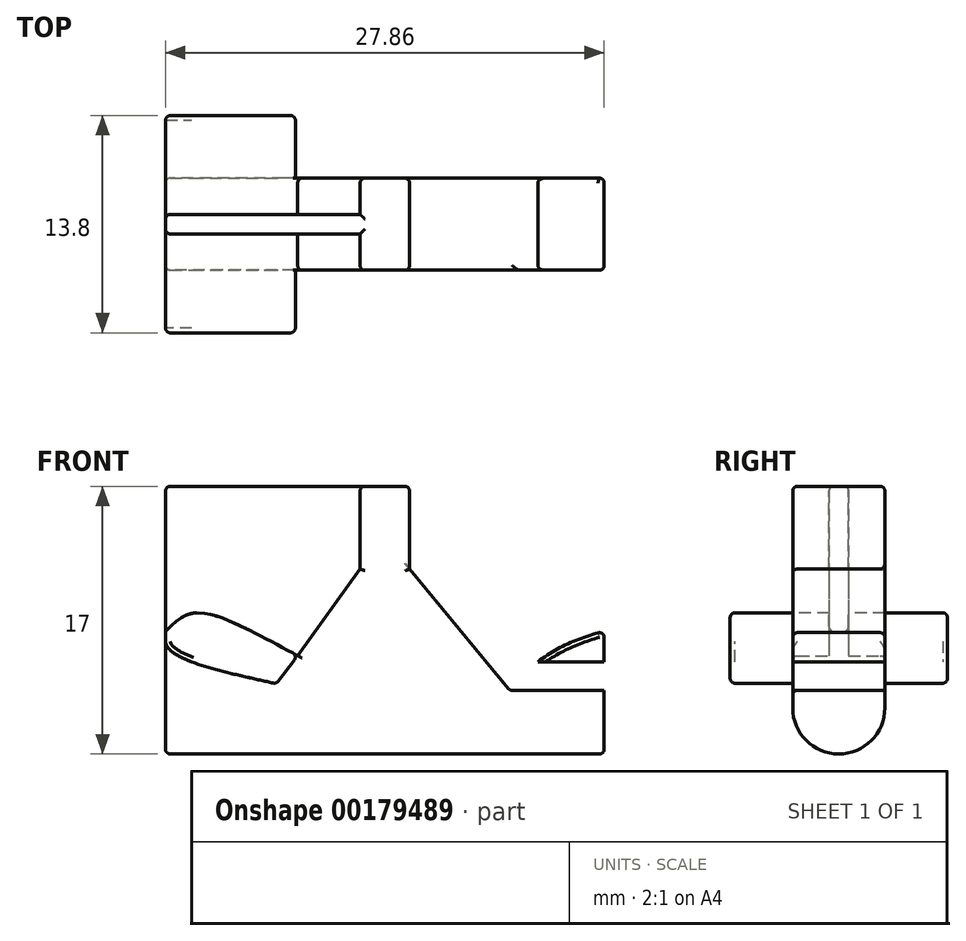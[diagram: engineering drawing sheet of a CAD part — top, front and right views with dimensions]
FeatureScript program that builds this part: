
annotation { "Feature Type Name" : "Feature", "Feature Type Description" : "" }
export const myFeature = defineFeature(function(context is Context, id is Id, definition is map)
    precondition{}
    {
        {
            var Q0;
            Q0=qCreatedBy(makeId("Front.planeOp"),FACE);
            var sketch = newSketch(context, id + "F0", { "sketchPlane" : qUnion([Q0])});
            skLineSegment(sketch, "E0.bottom", {"start": v(1.57, 8.26) * mm, "end": v(-1.57, 8.26) * mm});
            skLineSegment(sketch, "E0.top", {"start": v(1.57, 13.52) * mm, "end": v(-1.57, 13.52) * mm});
            skLineSegment(sketch, "E0.left", {"start": v(1.57, 8.26) * mm, "end": v(1.57, 13.52) * mm});
            skLineSegment(sketch, "E0.right", {"start": v(-1.57, 8.26) * mm, "end": v(-1.57, 13.52) * mm});
            skPoint(sketch, "E0.middle", {"position": v(0, 10.89) * mm});
            skLineSegment(sketch, "E1.bottom", {"start": v(13.93, -0.56) * mm, "end": v(-13.93, -0.56) * mm});
            skLineSegment(sketch, "E1.top", {"start": v(13.93, 0.56) * mm, "end": v(-13.93, 0.56) * mm});
            skLineSegment(sketch, "E1.left", {"start": v(13.93, -0.56) * mm, "end": v(13.93, 0.56) * mm});
            skLineSegment(sketch, "E1.right", {"start": v(-13.93, -0.56) * mm, "end": v(-13.93, 0.56) * mm});
            skPoint(sketch, "E1.middle", {"position": v(0, 0) * mm});
            skLineSegment(sketch, "E2", {"start": v(13.93, 0.56) * mm, "end": v(13.93, 4.32) * mm});
            skLineSegment(sketch, "E3", {"start": v(1.57, 8.26) * mm, "end": v(7.95, 0.56) * mm});
            skLineSegment(sketch, "E4", {"start": v(-1.57, 8.26) * mm, "end": v(-5.54, 2.76) * mm});
            skLineSegment(sketch, "E5", {"start": v(-13.93, 0.56) * mm, "end": v(-13.93, 4.32) * mm});
            skFitSpline(sketch, "E6", {"points": [v(-13.93, 4.32) * mm, v(-5.54, 2.76) * mm], "startDerivative": vector(5.32, 5.39) * mm, "endDerivative": vector(18.06, -9.8) * mm});
            skFitSpline(sketch, "E7", {"points": [v(7.95, 0.56) * mm, v(13.93, 4.32) * mm], "startDerivative": vector(5.08, 6.59) * mm, "endDerivative": vector(7.3, 1.91) * mm});
            skLineSegment(sketch, "E8.bottom", {"start": v(13.93, -3.48) * mm, "end": v(-13.93, -3.48) * mm});
            skLineSegment(sketch, "E8.top", {"start": v(13.93, 2.37) * mm, "end": v(-13.93, 2.37) * mm});
            skLineSegment(sketch, "E8.left", {"start": v(13.93, -3.48) * mm, "end": v(13.93, 2.37) * mm});
            skLineSegment(sketch, "E8.right", {"start": v(-13.93, -3.48) * mm, "end": v(-13.93, 2.37) * mm});
            skPoint(sketch, "E8.middle", {"position": v(0, -0.56) * mm});
            skLineSegment(sketch, "E9", {"start": v(-5.54, 2.76) * mm, "end": v(-6.9, 0.98) * mm});
            skFitSpline(sketch, "E10", {"points": [v(-13.93, 3.67) * mm, v(-6.9, 0.98) * mm], "startDerivative": vector(0, -3.91) * mm, "endDerivative": vector(7.3, -1.73) * mm});
            skLineSegment(sketch, "E11.bottom", {"start": v(-1.57, 13.52) * mm, "end": v(-13.93, 13.52) * mm});
            skLineSegment(sketch, "E11.top", {"start": v(-1.57, 0.56) * mm, "end": v(-13.93, 0.56) * mm});
            skLineSegment(sketch, "E11.left", {"start": v(-1.57, 13.52) * mm, "end": v(-1.57, 0.56) * mm});
            skLineSegment(sketch, "E11.right", {"start": v(-13.93, 13.52) * mm, "end": v(-13.93, 0.56) * mm});
            skSolve(sketch);
        }
        {
            var Q0;
            Q0=makeQuery(id+"F0.imprint","IMPRINT",FACE,{"disambiguationData":[TD([[makeQuery(id+"F0.imprint","IMPRINT",EDGE,{"derivedFrom":sQuery(id+"F0.wireOp",EDGE,"E0.bottom")}),-1.0]])]});
            var Q1;
            {var subQ6=sQuery(id+"F0.wireOp",EDGE,"E0.bottom");Q1=makeQuery(id+"F0.imprint","IMPRINT",FACE,{"disambiguationData":[TD([[makeQuery(id+"F0.imprint","IMPRINT",EDGE,{"derivedFrom":subQ6}),1.0]])]});}
            var Q2;
            {var subQ1=sQuery(id+"F0.wireOp",EDGE,"E8.top");var subQ5=sQuery(id+"F0.wireOp",EDGE,"E3");var subQ6=makeQuery(id+"F0.imprint","INTERSECT",VERTEX,{"derivedFrom":[subQ5,subQ1]});Q2=makeQuery(id+"F0.imprint","IMPRINT",FACE,{"disambiguationData":[TD([[makeQuery(id+"F0.imprint","IMPRINT",EDGE,{"disambiguationData":[TD([[subQ6,-1.0]])],"derivedFrom":subQ1}),1.0]])]});}
            var Q3;
            {var subQ0=sQuery(id+"F0.wireOp",EDGE,"E8.left");var subQ1=sQuery(id+"F0.wireOp",EDGE,"E1.top");var subQ2=makeQuery(id+"F0.imprint","INTERSECT",VERTEX,{"derivedFrom":[subQ1,subQ0]});Q3=makeQuery(id+"F0.imprint","IMPRINT",FACE,{"disambiguationData":[TD([[makeQuery(id+"F0.imprint","IMPRINT",EDGE,{"disambiguationData":[TD([[subQ2,-1.0]])],"derivedFrom":subQ1}),-1.0]])]});}
            var Q4;
            {var subQ1=sQuery(id+"F0.wireOp",EDGE,"E1.bottom");Q4=makeQuery(id+"F0.imprint","IMPRINT",FACE,{"disambiguationData":[TD([[makeQuery(id+"F0.imprint","IMPRINT",EDGE,{"derivedFrom":subQ1}),-1.0]])]});}
            var Q5;
            {var subQ1=sQuery(id+"F0.wireOp",EDGE,"E5");var subQ3=sQuery(id+"F0.wireOp",EDGE,"E10");var subQ4=makeQuery(id+"F0.imprint","INTERSECT",VERTEX,{"derivedFrom":[subQ1,subQ3]});Q5=makeQuery(id+"F0.imprint","IMPRINT",FACE,{"disambiguationData":[TD([[makeQuery(id+"F0.imprint","IMPRINT",EDGE,{"disambiguationData":[TD([[subQ4,-1.0]])],"derivedFrom":subQ3}),-1.0]])]});}
            var Q6;
            {var subQ0=sQuery(id+"F0.wireOp",EDGE,"E2");Q6=makeQuery(id+"F0.imprint","IMPRINT",FACE,{"disambiguationData":[TD([[makeQuery(id+"F0.imprint","IMPRINT",EDGE,{"derivedFrom":subQ0}),1.0]])]});}
            extrude(context, id + "F1", {"entities" : qUnion([Q0, Q1, Q2, Q3, Q4, Q5, Q6]), "endBound" : BoundingType.SYMMETRIC, "depth" : 5.85 * mm});
        }
        {
            var Q0;
            {var subQ5=sQuery(id+"F0.wireOp",EDGE,"E6");Q0=makeQuery(id+"F0.imprint","IMPRINT",FACE,{"disambiguationData":[TD([[makeQuery(id+"F0.imprint","IMPRINT",EDGE,{"derivedFrom":subQ5}),-1.0]])]});}
            var Q1;
            {var subQ0=sQuery(id+"F0.wireOp",EDGE,"E9");var subQ1=sQuery(id+"F0.wireOp",EDGE,"E8.top");var subQ2=makeQuery(id+"F0.imprint","INTERSECT",VERTEX,{"derivedFrom":[subQ1,subQ0]});Q1=makeQuery(id+"F0.imprint","IMPRINT",FACE,{"disambiguationData":[TD([[makeQuery(id+"F0.imprint","IMPRINT",EDGE,{"disambiguationData":[TD([[subQ2,-1.0]])],"derivedFrom":subQ1}),1.0]])]});}
            extrude(context, id + "F2", {"entities" : qUnion([Q0, Q1]), "operationType" : NewBodyOperationType.ADD, "endBound" : BoundingType.SYMMETRIC, "depth" : 13.8 * mm});
        }
        {
            var Q0;
            {var subQ0=sQuery(id+"F0.wireOp",EDGE,"E1.bottom");Q0=makeQuery(id+"F0.imprint","IMPRINT",FACE,{"disambiguationData":[TD([[makeQuery(id+"F0.imprint","IMPRINT",EDGE,{"derivedFrom":subQ0}),1.0]])]});}
            var Q1;
            Q1=sQuery(id+"F0.wireOp",EDGE,"E1.bottom");
            revolve(context, id + "F3", {"operationType" : NewBodyOperationType.ADD, "entities" : qUnion([Q0]), "axis" : qUnion([Q1]), "revolveType" : RevolveType.SYMMETRIC, "angle" : 180 * degree});
        }
        {
            var Q0;
            {var subQ4=sQuery(id+"F0.wireOp",EDGE,"E4");Q0=makeQuery(id+"F0.imprint","IMPRINT",FACE,{"disambiguationData":[TD([[makeQuery(id+"F0.imprint","IMPRINT",EDGE,{"derivedFrom":subQ4}),-1.0]])]});}
            extrude(context, id + "F4", {"entities" : qUnion([Q0]), "endBound" : BoundingType.SYMMETRIC, "depth" : 1.24 * mm});
        }
        {
            var Q0;
            {var subQ0=sQuery(id+"F0.wireOp",EDGE,"E4");Q0=makeQuery(id+"F0.imprint","IMPRINT",FACE,{"disambiguationData":[TD([[makeQuery(id+"F0.imprint","IMPRINT",EDGE,{"derivedFrom":subQ0}),1.0]])]});}
            var Q1;
            {var subQ10=sQuery(id+"F0.wireOp",EDGE,"E11.top");Q1=makeQuery(id+"F0.imprint","IMPRINT",FACE,{"disambiguationData":[TD([[makeQuery(id+"F0.imprint","IMPRINT",EDGE,{"derivedFrom":subQ10}),-1.0]])]});}
            extrude(context, id + "F5", {"entities" : qUnion([Q0, Q1]), "endBound" : BoundingType.SYMMETRIC, "depth" : 5.85 * mm});
        }
        {
            var Q0;
            Q0=makeQuery(id+"F5.opExtrude","SWEPT_BODY",BODY,{"disambiguationData":[OSD([sQuery(id+"F0.wireOp",EDGE,"E4"),sQuery(id+"F0.wireOp",EDGE,"E8.top"),sQuery(id+"F0.wireOp",EDGE,"E9"),sQuery(id+"F0.wireOp",EDGE,"E10"),sQuery(id+"F0.wireOp",EDGE,"E11.top"),sQuery(id+"F0.wireOp",EDGE,"E11.left"),sQuery(id+"F0.wireOp",EDGE,"E11.right")])]});
            var Q1;
            Q1=makeQuery(id+"F1.opExtrude","SWEPT_BODY",BODY,{"disambiguationData":[OSD([sQuery(id+"F0.wireOp",EDGE,"E8.top"),sQuery(id+"F0.wireOp",EDGE,"E10"),sQuery(id+"F0.wireOp",EDGE,"E11.right")])]});
            var Q2;
            Q2=makeQuery(id+"F1.opExtrude","SWEPT_BODY",BODY,{"disambiguationData":[OSD([sQuery(id+"F0.wireOp",EDGE,"E0.top"),sQuery(id+"F0.wireOp",EDGE,"E0.left"),sQuery(id+"F0.wireOp",EDGE,"E1.bottom"),sQuery(id+"F0.wireOp",EDGE,"E2"),sQuery(id+"F0.wireOp",EDGE,"E3"),sQuery(id+"F0.wireOp",EDGE,"E7"),sQuery(id+"F0.wireOp",EDGE,"E8.left"),sQuery(id+"F0.wireOp",EDGE,"E8.right"),sQuery(id+"F0.wireOp",EDGE,"E11.top"),sQuery(id+"F0.wireOp",EDGE,"E11.left")])]});
            var Q3;
            Q3=makeQuery(id+"F2.opExtrude","SWEPT_BODY",BODY,{"disambiguationData":[OSD([sQuery(id+"F0.wireOp",EDGE,"E6"),sQuery(id+"F0.wireOp",EDGE,"E9"),sQuery(id+"F0.wireOp",EDGE,"E10"),sQuery(id+"F0.wireOp",EDGE,"E11.right")])]});
            var Q4;
            Q4=makeQuery(id+"F4.opExtrude","SWEPT_BODY",BODY,{"disambiguationData":[OSD([sQuery(id+"F0.wireOp",EDGE,"E4"),sQuery(id+"F0.wireOp",EDGE,"E6"),sQuery(id+"F0.wireOp",EDGE,"E11.bottom"),sQuery(id+"F0.wireOp",EDGE,"E11.left"),sQuery(id+"F0.wireOp",EDGE,"E11.right")])]});
            booleanBodies(context, id + "F6", {"operationType" : BooleanOperationType.UNION, "tools" : qUnion([Q0, Q1, Q2, Q3, Q4])});
        }
        {
            var Q0;
            {var subQ0=sQuery(id+"F0.wireOp",EDGE,"E11.right");var subQ1=sQuery(id+"F0.wireOp",EDGE,"E6");Q0=makeQuery(id+"F6.opBoolean","SPLIT",EDGE,{"disambiguationData":[TD([makeQuery(id+"F2.opExtrude","CAP_FACE",FACE,{"disambiguationData":[OSD([subQ1,sQuery(id+"F0.wireOp",EDGE,"E9"),sQuery(id+"F0.wireOp",EDGE,"E10"),subQ0])],"isStart":false})])],"derivedFrom":makeQuery(id+"F2.opExtrude","SWEPT_EDGE",EDGE,{"disambiguationData":[OSD([subQ1,subQ0])]})});}
            var Q1;
            {var subQ0=sQuery(id+"F0.wireOp",EDGE,"E6");var subQ1=sQuery(id+"F0.wireOp",EDGE,"E11.right");Q1=makeQuery(id+"F6.opBoolean","SPLIT",EDGE,{"disambiguationData":[TD([makeQuery(id+"F2.opExtrude","CAP_FACE",FACE,{"disambiguationData":[OSD([subQ0,sQuery(id+"F0.wireOp",EDGE,"E9"),sQuery(id+"F0.wireOp",EDGE,"E10"),subQ1])],"isStart":true})])],"derivedFrom":makeQuery(id+"F2.opExtrude","SWEPT_EDGE",EDGE,{"disambiguationData":[OSD([subQ0,subQ1])]})});}
            var Q2;
            Q2=makeQuery(id+"F4.opExtrude","SWEPT_EDGE",EDGE,{"disambiguationData":[OSD([sQuery(id+"F0.wireOp",EDGE,"E11.bottom"),sQuery(id+"F0.wireOp",EDGE,"E11.right")])]});
            var Q3;
            Q3=makeQuery(id+"F4.opExtrude","CAP_EDGE",EDGE,{"disambiguationData":[OSD([sQuery(id+"F0.wireOp",EDGE,"E11.right")])],"isStart":false});
            var Q4;
            Q4=makeQuery(id+"F4.opExtrude","CAP_EDGE",EDGE,{"disambiguationData":[OSD([sQuery(id+"F0.wireOp",EDGE,"E11.bottom")])],"isStart":false});
            var Q5;
            {var subQ0=sQuery(id+"F0.wireOp",EDGE,"E11.left");var subQ1=sQuery(id+"F0.wireOp",EDGE,"E11.right");var subQ3=sQuery(id+"F0.wireOp",EDGE,"E10");var subQ4=sQuery(id+"F0.wireOp",EDGE,"E8.top");var subQ6=sQuery(id+"F0.wireOp",EDGE,"E0.top");var subQ7=sQuery(id+"F0.wireOp",EDGE,"E11.bottom");Q5=makeQuery(id+"F6.opBoolean","SPLIT",EDGE,{"disambiguationData":[TD([makeQuery(id+"F1.opExtrude","CAP_FACE",FACE,{"disambiguationData":[OSD([subQ4,subQ3,subQ1])],"isStart":false})])],"derivedFrom":makeQuery(id+"F1.opExtrude","SWEPT_EDGE",EDGE,{"disambiguationData":[OSD([subQ6,subQ7,subQ0])]})});}
            var Q6;
            {var subQ0=sQuery(id+"F0.wireOp",EDGE,"E11.left");var subQ1=sQuery(id+"F0.wireOp",EDGE,"E11.right");var subQ2=sQuery(id+"F0.wireOp",EDGE,"E10");var subQ3=sQuery(id+"F0.wireOp",EDGE,"E8.top");var subQ5=sQuery(id+"F0.wireOp",EDGE,"E0.top");var subQ6=sQuery(id+"F0.wireOp",EDGE,"E11.bottom");Q6=makeQuery(id+"F6.opBoolean","SPLIT",EDGE,{"disambiguationData":[TD([makeQuery(id+"F1.opExtrude","CAP_FACE",FACE,{"disambiguationData":[OSD([subQ3,subQ2,subQ1])],"isStart":true})])],"derivedFrom":makeQuery(id+"F1.opExtrude","SWEPT_EDGE",EDGE,{"disambiguationData":[OSD([subQ5,subQ6,subQ0])]})});}
            var Q7;
            Q7=makeQuery(id+"F1.opExtrude","CAP_EDGE",EDGE,{"disambiguationData":[OSD([sQuery(id+"F0.wireOp",EDGE,"E0.top")])],"isStart":false});
            var Q8;
            Q8=makeQuery(id+"F1.opExtrude","SWEPT_EDGE",EDGE,{"disambiguationData":[OSD([sQuery(id+"F0.wireOp",EDGE,"E0.top"),sQuery(id+"F0.wireOp",EDGE,"E0.left")])]});
            var Q9;
            Q9=makeQuery(id+"F1.opExtrude","CAP_EDGE",EDGE,{"disambiguationData":[OSD([sQuery(id+"F0.wireOp",EDGE,"E0.top")])],"isStart":true});
            var Q10;
            Q10=makeQuery(id+"F2.opExtrude","CAP_EDGE",EDGE,{"disambiguationData":[OSD([sQuery(id+"F0.wireOp",EDGE,"E6")])],"isStart":false});
            var Q11;
            Q11=makeQuery(id+"F2.opExtrude","CAP_EDGE",EDGE,{"disambiguationData":[OSD([sQuery(id+"F0.wireOp",EDGE,"E6")])],"isStart":true});
            var Q12;
            Q12=makeQuery(id+"F2.opExtrude","CAP_EDGE",EDGE,{"disambiguationData":[OSD([sQuery(id+"F0.wireOp",EDGE,"E9")])],"isStart":true});
            var Q13;
            Q13=makeQuery(id+"F2.opExtrude","CAP_EDGE",EDGE,{"disambiguationData":[OSD([sQuery(id+"F0.wireOp",EDGE,"E10")])],"isStart":true});
            var Q14;
            Q14=makeQuery(id+"F2.opExtrude","CAP_EDGE",EDGE,{"disambiguationData":[OSD([sQuery(id+"F0.wireOp",EDGE,"E11.right")])],"isStart":true});
            var Q15;
            Q15=makeQuery(id+"F2.opExtrude","CAP_EDGE",EDGE,{"disambiguationData":[OSD([sQuery(id+"F0.wireOp",EDGE,"E11.right")])],"isStart":false});
            var Q16;
            Q16=makeQuery(id+"F2.opExtrude","CAP_EDGE",EDGE,{"disambiguationData":[OSD([sQuery(id+"F0.wireOp",EDGE,"E10")])],"isStart":false});
            var Q17;
            Q17=makeQuery(id+"F2.opExtrude","CAP_EDGE",EDGE,{"disambiguationData":[OSD([sQuery(id+"F0.wireOp",EDGE,"E9")])],"isStart":false});
            var Q18;
            {var subQ0=sQuery(id+"F0.wireOp",EDGE,"E11.right");var subQ1=sQuery(id+"F0.wireOp",EDGE,"E10");var subQ2=sQuery(id+"F0.wireOp",EDGE,"E9");var subQ5=sQuery(id+"F0.wireOp",EDGE,"E8.top");Q18=makeQuery(id+"F6.opBoolean","SPLIT",EDGE,{"disambiguationData":[TD([makeQuery(id+"F1.opExtrude","CAP_FACE",FACE,{"disambiguationData":[OSD([subQ5,subQ1,subQ0])],"isStart":false})])],"derivedFrom":makeQuery(id+"F2.opExtrude","SWEPT_EDGE",EDGE,{"disambiguationData":[OSD([subQ2,subQ1])]})});}
            var Q19;
            {var subQ0=sQuery(id+"F0.wireOp",EDGE,"E11.right");var subQ1=sQuery(id+"F0.wireOp",EDGE,"E10");var subQ2=sQuery(id+"F0.wireOp",EDGE,"E9");var subQ3=sQuery(id+"F0.wireOp",EDGE,"E6");var subQ6=sQuery(id+"F0.wireOp",EDGE,"E8.top");var subQ7=sQuery(id+"F0.wireOp",EDGE,"E4");Q19=makeQuery(id+"F6.opBoolean","SPLIT",EDGE,{"disambiguationData":[TD([makeQuery(id+"F1.opExtrude","CAP_FACE",FACE,{"disambiguationData":[OSD([subQ6,subQ1,subQ0])],"isStart":false})])],"derivedFrom":makeQuery(id+"F2.opExtrude","SWEPT_EDGE",EDGE,{"disambiguationData":[OSD([subQ7,subQ3,subQ2])]})});}
            var Q20;
            {var subQ0=sQuery(id+"F0.wireOp",EDGE,"E9");var subQ1=sQuery(id+"F0.wireOp",EDGE,"E11.right");var subQ2=sQuery(id+"F0.wireOp",EDGE,"E10");var subQ3=sQuery(id+"F0.wireOp",EDGE,"E8.top");Q20=makeQuery(id+"F6.opBoolean","SPLIT",EDGE,{"disambiguationData":[TD([makeQuery(id+"F1.opExtrude","CAP_FACE",FACE,{"disambiguationData":[OSD([subQ3,subQ2,subQ1])],"isStart":true})])],"derivedFrom":makeQuery(id+"F2.opExtrude","SWEPT_EDGE",EDGE,{"disambiguationData":[OSD([subQ0,subQ2])]})});}
            var Q21;
            {var subQ0=sQuery(id+"F0.wireOp",EDGE,"E11.right");var subQ1=sQuery(id+"F0.wireOp",EDGE,"E10");var subQ2=sQuery(id+"F0.wireOp",EDGE,"E9");var subQ3=sQuery(id+"F0.wireOp",EDGE,"E6");var subQ4=sQuery(id+"F0.wireOp",EDGE,"E8.top");var subQ7=sQuery(id+"F0.wireOp",EDGE,"E4");Q21=makeQuery(id+"F6.opBoolean","SPLIT",EDGE,{"disambiguationData":[TD([makeQuery(id+"F1.opExtrude","CAP_FACE",FACE,{"disambiguationData":[OSD([subQ4,subQ1,subQ0])],"isStart":true})])],"derivedFrom":makeQuery(id+"F2.opExtrude","SWEPT_EDGE",EDGE,{"disambiguationData":[OSD([subQ7,subQ3,subQ2])]})});}
            var Q22;
            Q22=makeQuery(id+"F1.opExtrude","SWEPT_EDGE",EDGE,{"disambiguationData":[OSD([sQuery(id+"F0.wireOp",EDGE,"E2"),sQuery(id+"F0.wireOp",EDGE,"E7")])]});
            var Q23;
            Q23=makeQuery(id+"F1.opExtrude","SWEPT_EDGE",EDGE,{"disambiguationData":[OSD([sQuery(id+"F0.wireOp",EDGE,"E1.top"),sQuery(id+"F0.wireOp",EDGE,"E3"),sQuery(id+"F0.wireOp",EDGE,"E7")])]});
            var Q24;
            Q24=makeQuery(id+"F1.opExtrude","CAP_EDGE",EDGE,{"disambiguationData":[OSD([sQuery(id+"F0.wireOp",EDGE,"E7")])],"isStart":true});
            var Q25;
            Q25=makeQuery(id+"F1.opExtrude","CAP_EDGE",EDGE,{"disambiguationData":[OSD([sQuery(id+"F0.wireOp",EDGE,"E3")])],"isStart":false});
            fillet(context, id + "F7", {"entities" : qUnion([Q0, Q1, Q2, Q3, Q4, Q5, Q6, Q7, Q8, Q9, Q10, Q11, Q12, Q13, Q14, Q15, Q16, Q17, Q18, Q19, Q20, Q21, Q22, Q23, Q24, Q25]), "radius" : .3 * mm, "tangentPropagation" : true, "allowEdgeOverflow" : false});
        }
        {
            var Q0;
            Q0=makeQuery(id+"F4.opExtrude","CAP_EDGE",EDGE,{"disambiguationData":[OSD([sQuery(id+"F0.wireOp",EDGE,"E11.bottom")])],"isStart":true});
            var Q1;
            Q1=makeQuery(id+"F4.opExtrude","CAP_EDGE",EDGE,{"disambiguationData":[OSD([sQuery(id+"F0.wireOp",EDGE,"E11.right")])],"isStart":true});
            fillet(context, id + "F8", {"entities" : qUnion([Q0, Q1]), "radius" : .3 * mm, "tangentPropagation" : true, "allowEdgeOverflow" : false});
        }
        {
            var Q0;
            Q0=makeQuery(id+"F5.opExtrude","CAP_EDGE",EDGE,{"disambiguationData":[OSD([sQuery(id+"F0.wireOp",EDGE,"E4")])],"isStart":true});
            fillet(context, id + "F9", {"entities" : qUnion([Q0]), "radius" : .3 * mm, "tangentPropagation" : true, "allowEdgeOverflow" : false});
        }
        {
            var Q0;
            Q0=makeQuery(id+"F5.opExtrude","CAP_EDGE",EDGE,{"disambiguationData":[OSD([sQuery(id+"F0.wireOp",EDGE,"E4")])],"isStart":false});
            var Q1;
            Q1=makeQuery(id+"F1.opExtrude","CAP_EDGE",EDGE,{"disambiguationData":[OSD([sQuery(id+"F0.wireOp",EDGE,"E11.left")])],"isStart":false});
            var Q2;
            Q2=makeQuery(id+"F1.opExtrude","CAP_EDGE",EDGE,{"disambiguationData":[OSD([sQuery(id+"F0.wireOp",EDGE,"E11.left")])],"isStart":true});
            fillet(context, id + "F10", {"entities" : qUnion([Q0, Q1, Q2]), "radius" : .3 * mm, "tangentPropagation" : true, "allowEdgeOverflow" : false});
        }
        {
            var Q0;
            Q0=makeQuery(id+"F1.opExtrude","CAP_EDGE",EDGE,{"disambiguationData":[OSD([sQuery(id+"F0.wireOp",EDGE,"E0.left")])],"isStart":false});
            var Q1;
            Q1=makeQuery(id+"F1.opExtrude","CAP_EDGE",EDGE,{"disambiguationData":[OSD([sQuery(id+"F0.wireOp",EDGE,"E0.left")])],"isStart":true});
            fillet(context, id + "F11", {"entities" : qUnion([Q0, Q1]), "radius" : .3 * mm, "tangentPropagation" : true, "allowEdgeOverflow" : false});
        }
        {
            var Q0;
            Q0=makeQuery(id+"F1.opExtrude","CAP_EDGE",EDGE,{"disambiguationData":[OSD([sQuery(id+"F0.wireOp",EDGE,"E2"),sQuery(id+"F0.wireOp",EDGE,"E8.left")])],"isStart":false});
            var Q1;
            Q1=makeQuery(id+"F1.opExtrude","CAP_EDGE",EDGE,{"disambiguationData":[OSD([sQuery(id+"F0.wireOp",EDGE,"E2"),sQuery(id+"F0.wireOp",EDGE,"E8.left")])],"isStart":true});
            var Q2;
            Q2=makeQuery(id+"F3.opRevolve","SWEPT_EDGE",EDGE,{"disambiguationData":[OSD([sQuery(id+"F0.wireOp",EDGE,"E8.bottom"),sQuery(id+"F0.wireOp",EDGE,"E8.left")])]});
            var Q3;
            {var subQ0=sQuery(id+"F0.wireOp",EDGE,"E11.right");Q3=makeQuery(id+"F6.opBoolean","MERGE",EDGE,{"derivedFrom":[makeQuery(id+"F1.opExtrude","CAP_EDGE",EDGE,{"disambiguationData":[OSD([sQuery(id+"F0.wireOp",EDGE,"E8.right")])],"isStart":false}),makeQuery(id+"F1.opExtrude","CAP_EDGE",EDGE,{"disambiguationData":[OSD([subQ0])],"isStart":false}),makeQuery(id+"F5.opExtrude","CAP_EDGE",EDGE,{"disambiguationData":[OSD([subQ0])],"isStart":false})]});}
            var Q4;
            Q4=makeQuery(id+"F3.opRevolve","SWEPT_EDGE",EDGE,{"disambiguationData":[OSD([sQuery(id+"F0.wireOp",EDGE,"E8.bottom"),sQuery(id+"F0.wireOp",EDGE,"E8.right")])]});
            var Q5;
            {var subQ0=sQuery(id+"F0.wireOp",EDGE,"E11.right");Q5=makeQuery(id+"F6.opBoolean","MERGE",EDGE,{"derivedFrom":[makeQuery(id+"F1.opExtrude","CAP_EDGE",EDGE,{"disambiguationData":[OSD([sQuery(id+"F0.wireOp",EDGE,"E8.right")])],"isStart":true}),makeQuery(id+"F1.opExtrude","CAP_EDGE",EDGE,{"disambiguationData":[OSD([subQ0])],"isStart":true}),makeQuery(id+"F5.opExtrude","CAP_EDGE",EDGE,{"disambiguationData":[OSD([subQ0])],"isStart":true})]});}
            fillet(context, id + "F12", {"entities" : qUnion([Q0, Q1, Q2, Q3, Q4, Q5]), "radius" : .3 * mm, "tangentPropagation" : true, "allowEdgeOverflow" : false});
        }
    });
